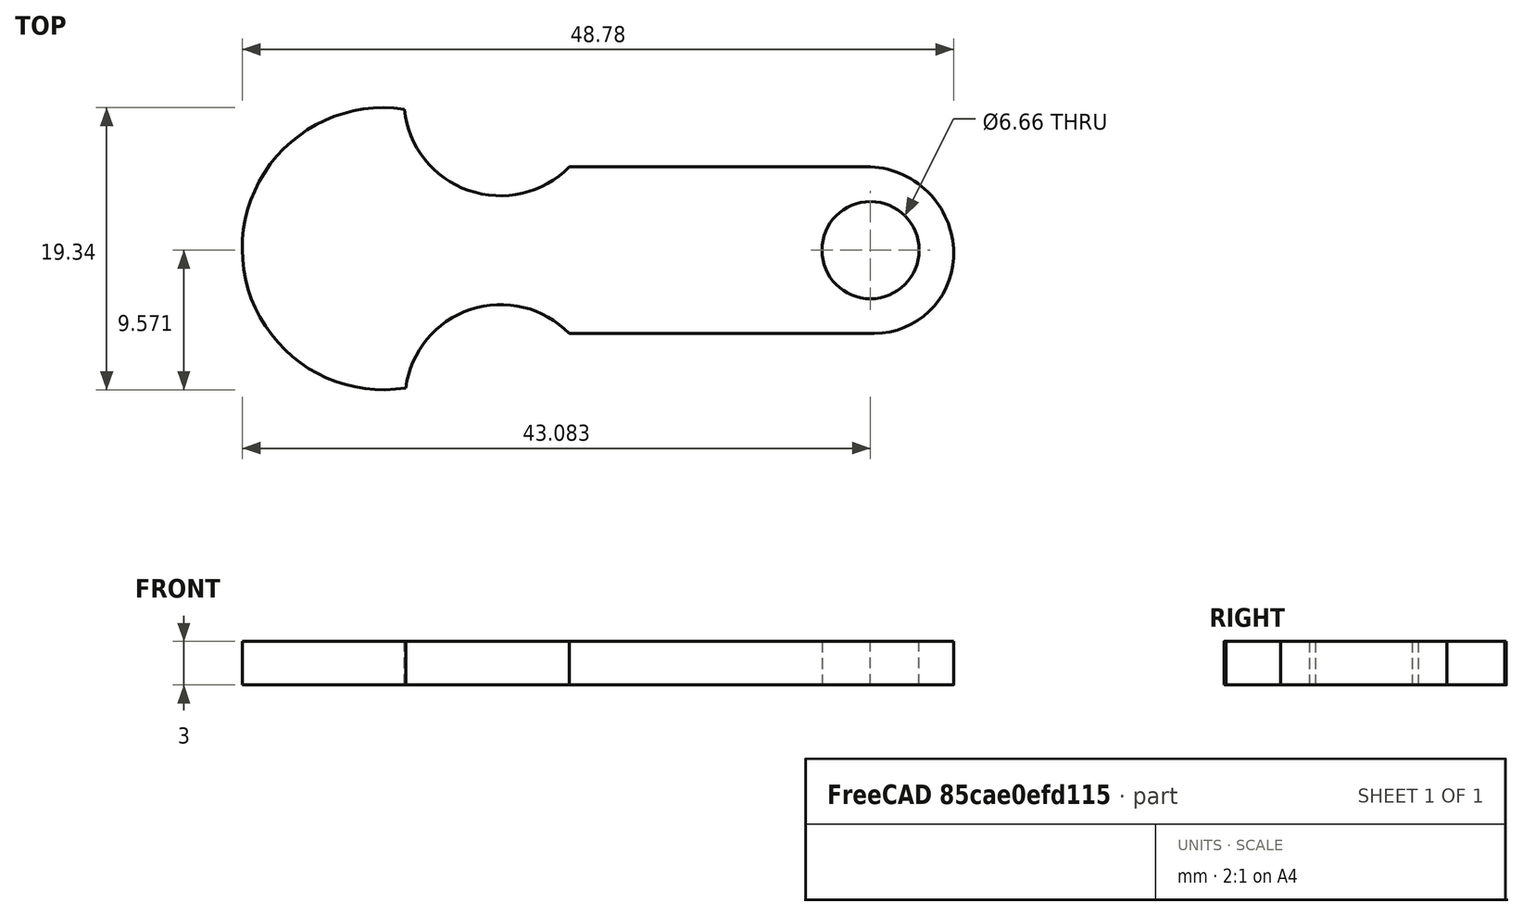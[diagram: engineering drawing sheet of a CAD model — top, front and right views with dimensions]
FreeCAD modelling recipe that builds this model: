
FCSTD DOCUMENT  (FreeCAD 1.1R14555 (Git shallow))
Label: shoppingtrolleytoken
License: All rights reserved
LicenseURL: https://en.wikipedia.org/wiki/All_rights_reserved
objects: Part::Feature×4, Mesh::Feature×1, PartDesign::SubShapeBinder×1, App::Point×1, Sketcher::SketchObject×1, PartDesign::Pad×1, PartDesign::Body×1
note: 11 computed .brp shape members not serialized (recipe doc carries the construction recipe); baked Part::Feature solids carry a one-line shape summary decoded from their .brp

FEATURE [Mesh::Feature] twodollartokeninstructables_scaled_952  label="twodollartokeninstructables-scaled-952"
FEATURE [Part::Feature] twodollartokeninstructables_scaled_952_cs
  shape: bbox 48.79 x 19.52 x 2e-07 mm, 0 faces, 0 solids (baked)
FEATURE [Part::Feature] twodollartokeninstructables_scaled_952_cs001
  shape: bbox 48.79 x 6.768e-07 x 2.951 mm, 0 faces, 0 solids (baked)
FEATURE [Part::Feature] twodollartokeninstructables_scaled_952_cs002
  shape: bbox 2e-07 x 11.42 x 2.951 mm, 0 faces, 0 solids (baked)
FEATURE [Part::Feature] twodollartokeninstructables_scaled_952_cs003
  shape: bbox 2e-07 x 11.42 x 2.951 mm, 0 faces, 0 solids (baked)
FEATURE [PartDesign::SubShapeBinder] Binder001
  BindCopyOnChange = 0
  BindMode = 0
  ClaimChildren = false
  Fuse = false
  MakeFace = true
  OffsetFill = false
  OffsetIntersection = false
  OffsetJoinType = 0
  OffsetOpenResult = false
  PartialLoad = false
  Refine = true
  Relative = true
  Support = -> [twodollartokeninstructables_scaled_952_cs[Edge289,Edge290,Edge291,Edge292,Edge293,Edge294,Edge295,Edge296]]
  _Version = 2
FEATURE [App::Point] Origin001
  Role = Origin
FEATURE [Sketcher::SketchObject] Sketch
  ArcFitTolerance = 1e-06
  AttachmentSupport = -> [Origin]
  ExternalGeometry = -> [Binder001]
  ExternalTypes = [0,0,0,0,0,0,0,0,0,0,0,0,0]
  FullyConstrained = true
  MakeInternals = false
  MapMode = 5
  sketch-geometry (8):
    g0: LineSegment StartX=-1.96807 StartY=-5.712 StartZ=0 EndX=18.9322 EndY=-5.70656 EndZ=0
    g1: ArcOfCircle CenterX=18.9307 CenterY=-0.258787 CenterZ=0 NormalX=0 NormalY=0 NormalZ=1 AngleXU=0 Radius=5.44778 StartAngle=4.71265 EndAngle=6.23929
    g2: ArcOfCircle CenterX=18.4248 CenterY=-0.236567 CenterZ=0 NormalX=0 NormalY=0 NormalZ=1 AngleXU=0 Radius=5.95417 StartAngle=6.23929 EndAngle=7.81061
    g3: LineSegment StartX=18.683 StartY=5.712 StartZ=0 EndX=-1.96807 EndY=5.712 EndZ=0
    g4: ArcOfCircle CenterX=-6.69473 CenterY=10.3585 CenterZ=0 NormalX=0 NormalY=0 NormalZ=1 AngleXU=0 Radius=6.62806 StartAngle=3.24677 EndAngle=5.50634
    g5: ArcOfCircle CenterX=-6.66882 CenterY=-10.3006 CenterZ=0 NormalX=0 NormalY=0 NormalZ=1 AngleXU=0 Radius=6.56902 StartAngle=0.773321 EndAngle=3.01106
    g6: ArcOfCircle CenterX=-14.7255 CenterY=0.100429 CenterZ=0 NormalX=0 NormalY=0 NormalZ=1 AngleXU=0 Radius=9.66993 StartAngle=1.42139 EndAngle=4.8727
    g7: Circle CenterX=18.6831 CenterY=0.000541823 CenterZ=0 NormalX=0 NormalY=0 NormalZ=1 AngleXU=0 Radius=3.33157
  constraints (20):
    c: Coincident(g-5,g0)
    c: Coincident(g0,g-6)
    c: Tangent(g0,g1) = -1.5708
    c: Coincident(g1,g-15)
    c: Tangent(g1,g2) = -1.5708
    c: Coincident(g2,g-4)
    c: Coincident(g3,g2)
    c: Coincident(g3,g-3)
    c: Coincident(g4,g3)
    c: Coincident(g4,g-10)
    c: PointOnObject(g-9,g4)
    c: Coincident(g5,g0)
    c: Coincident(g5,g-7)
    c: PointOnObject(g-8,g5)
    c: Coincident(g6,g5)
    c: Coincident(g6,g4)
    c: PointOnObject(g-11,g6)
    c: PointOnObject(g-13,g7)
    c: PointOnObject(g-14,g7)
    c: PointOnObject(g-12,g7)
FEATURE [PartDesign::Pad] Pad
  Direction = (0,0,1)
  Length = 3
  Length2 = 10
  Profile = -> Sketch
  ReferenceAxis = -> Sketch [N_Axis]
  Refine = true
  SideType = 0
  Suppressed = false
  Type = 0
  Type2 = 0
FEATURE [PartDesign::Body] Body
  AllowCompound = true
  Group = -> [Sketch,Binder001,Pad]
  Origin = -> Origin
  Tip = -> Pad
